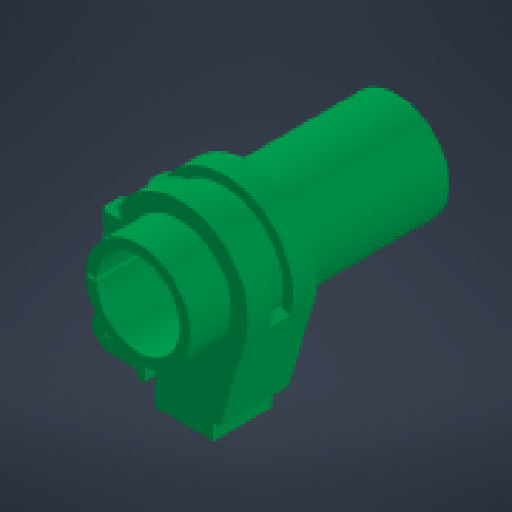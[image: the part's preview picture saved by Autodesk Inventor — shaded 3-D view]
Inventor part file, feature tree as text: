
AUTODESK INVENTOR PART (.ipt)
format: ipt  version: 2024 (Build 280153000, 153)  size: 458,752 bytes
history: native  units: mm
features: other x16, sketch x15, extrude x12, fillet x4, mirror x3, projected_geometry x3, reference x2, shell x1, sweep x1
ambient origin geometry x8: Origin, YZ Plane, XZ Plane, XY Plane, X Axis, Y Axis, Z Axis, Center Point
bodies: Body1 (feature_tree)
feature tree (57):
  other  "Твердое тело1"
  extrude  "Выдавливание1"  Depth=20.0mm
  shell  "Оболочка1"  Thickness=1.5mm
  extrude  "Выдавливание2"  Depth=20.0mm TaperAngle=0.0deg
  other  "РабПлоскость1"
  extrude  "Выдавливание4"  Depth=4.0mm
  sketch  "Эскиз8"
  other  "РабПлоскость3"
  sweep  "Сдвиг1"
  other  "РабОсь1"
  other  "РабПлоскость4"
  fillet  "Сопряжение2"  Radius=5.0mm
  other  "РабПлоскость5"
  other  "РабПлоскость6"
  other  "РабПлоскость7"
  other  "РабПлоскость8"
  extrude  "Выдавливание18"  Depth=20.0mm TaperAngle=0.0deg
  extrude  "Выдавливание19"  Depth=20.2mm
  extrude  "Выдавливание20"  Depth=24.4mm
  mirror  "Зеркальное отражение7"
  other  "Непосредственное редактирование3"
  fillet  "Сопряжение9"  Radius=8.0mm
  fillet  "Сопряжение10"  [1 undecoded]
  other  "Непосредственное редактирование4"
  extrude  "Выдавливание22"  Depth=3.0mm
  mirror  "Зеркальное отражение8"
  extrude  "Выдавливание23"  Depth=6.0mm
  extrude  "Выдавливание24"  Depth=1.0mm
  extrude  "Выдавливание25"  Depth=6.0mm
  mirror  "Зеркальное отражение9"
  extrude  "Выдавливание26"  Depth=16.25mm TaperAngle=0.0deg
  fillet  "Сопряжение11"  Radius=3.0mm
  extrude  "Выдавливание27"  Depth=18.5mm TaperAngle=0.0deg
  sketch  "Эскиз1"
  sketch  "Эскиз2"
  projected_geometry  "Спроецированная петля1"
  sketch  "Эскиз5"
  reference  "Ссылка3"
  reference  "Ссылка4"
  sketch  "Эскиз10"
  sketch  "3D эскиз1"
  sketch  "Эскиз32"
  sketch  "Эскиз33"
  sketch  "Эскиз35"
  sketch  "Эскиз37"
  sketch  "Эскиз39"
  sketch  "Эскиз40"
  projected_geometry  "Спроецированная петля3"
  sketch  "Эскиз41"
  sketch  "Эскиз42"
  sketch  "Эскиз43"
  projected_geometry  "Спроецированная петля4"
  parser-record x1  (decoder bookkeeping rows leaked as tree rows — omitted from the tree; the rows remain in map.json)
  other  "arm_assembly.iam"
  other  "arm:1"
  other  "Перенос3"
  other  "Перенос4"
note: 1 required parameter value undecoded (feature->parameter linkage not recoverable at this tier; creation-order binding heuristic only, values carry confidence <= 0.55)
note: 1 file-system path scrubbed to <path> (originals preserved in map.json)
